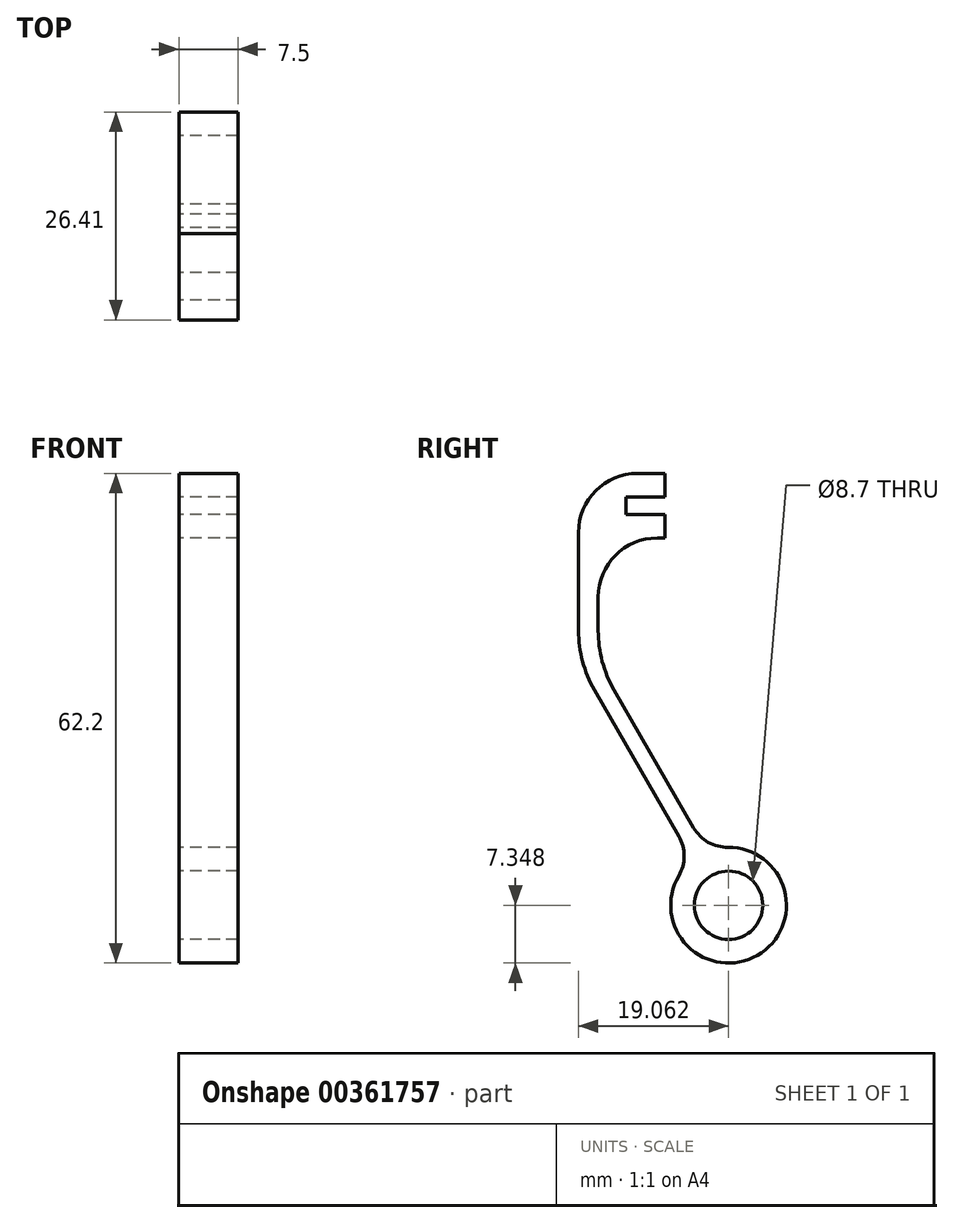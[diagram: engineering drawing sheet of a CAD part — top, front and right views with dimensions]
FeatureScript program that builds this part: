
annotation { "Feature Type Name" : "Feature", "Feature Type Description" : "" }
export const myFeature = defineFeature(function(context is Context, id is Id, definition is map)
    precondition{}
    {
        {
            var Q0;
            Q0=qCreatedBy(makeId("Right.planeOp"),FACE);
            var sketch = newSketch(context, id + "F0", { "sketchPlane" : qUnion([Q0])});
            skLineSegment(sketch, "E0", {"start": v(0, 18.8) * mm, "end": v(-5, 18.8) * mm});
            skLineSegment(sketch, "E1", {"start": v(-5, 18.8) * mm, "end": v(-5, 21) * mm});
            skLineSegment(sketch, "E2", {"start": v(-5, 21) * mm, "end": v(0, 21) * mm});
            skLineSegment(sketch, "E3", {"start": v(0, 21) * mm, "end": v(0, 24) * mm});
            skLineSegment(sketch, "E4", {"start": v(0, 24) * mm, "end": v(-11, 24) * mm});
            skLineSegment(sketch, "E5", {"start": v(0, 18.8) * mm, "end": v(0, 15.8) * mm});
            skLineSegment(sketch, "E6", {"start": v(0, 15.8) * mm, "end": v(-8.5, 15.8) * mm});
            skLineSegment(sketch, "E7", {"start": v(-8.5, 15.8) * mm, "end": v(-8.5, 4.02) * mm});
            skLineSegment(sketch, "E8", {"start": v(-6.5, -3.48) * mm, "end": v(3.63, -21) * mm});
            skLineSegment(sketch, "E9", {"start": v(-11, 24) * mm, "end": v(-11, 4.02) * mm});
            skLineSegment(sketch, "E10", {"start": v(-9, -3.48) * mm, "end": v(1.75, -22.09) * mm});
            skPoint(sketch, "E11.start.orphan", {"position": v(-16.86, 0) * mm});
            skPoint(sketch, "E12.orphan", {"position": v(6.83, -31.85) * mm});
            skPoint(sketch, "E13.orphan", {"position": v(7.4, -31.85) * mm});
            skCircle(sketch, "E14", {"center": v(8.06, -30.85) * mm, "radius": 4.35 * mm});
            skArc(sketch, "E15.0", {"start": v(1.73, -27.12) * mm, "mid": v(11.74, -37.22) * mm, "end": v(8, -23.5) * mm});
            skPoint(sketch, "E16.orphan", {"position": v(9, -30.31) * mm});
            skPoint(sketch, "E17.end.orphan", {"position": v(7.13, -31.4) * mm});
            skPoint(sketch, "E18.visualSharp", {"position": v(3.5, -25.1) * mm});
            skArc(sketch, "E18.filletArc", {"start": v(1.73, -27.12) * mm, "mid": v(2.42, -24.6) * mm, "end": v(1.75, -22.09) * mm});
            skPoint(sketch, "E19.visualSharp", {"position": v(5.37, -24.02) * mm});
            skArc(sketch, "E19.filletArc", {"start": v(3.63, -21) * mm, "mid": v(5.47, -22.84) * mm, "end": v(8, -23.5) * mm});
            skPoint(sketch, "E20.visualSharp", {"position": v(-8.5, 0) * mm});
            skArc(sketch, "E20.filletArc", {"start": v(-8.5, 4.02) * mm, "mid": v(-7.99, 0.14) * mm, "end": v(-6.5, -3.48) * mm});
            skPoint(sketch, "E21.visualSharp", {"position": v(-11, 0) * mm});
            skArc(sketch, "E21.filletArc", {"start": v(-11, 4.02) * mm, "mid": v(-10.49, 0.14) * mm, "end": v(-9, -3.48) * mm});
            skSolve(sketch);
        }
        {
            var Q0;
            Q0=makeQuery(id+"F0.imprint","IMPRINT",FACE,{"disambiguationData":[TD([[makeQuery(id+"F0.imprint","IMPRINT",EDGE,{"derivedFrom":sQuery(id+"F0.wireOp",EDGE,"E0")}),1.0]])]});
            extrude(context, id + "F1", {"entities" : qUnion([Q0]), "depth" : 7.5 * mm, "offsetDistance" : 25 * mm});
        }
        {
            var Q0;
            Q0=makeQuery(id+"F1.opExtrude","SWEPT_EDGE",EDGE,{"disambiguationData":[OSD([sQuery(id+"F0.wireOp",EDGE,"E4"),sQuery(id+"F0.wireOp",EDGE,"E9")])]});
            var Q1;
            Q1=makeQuery(id+"F1.opExtrude","SWEPT_EDGE",EDGE,{"disambiguationData":[OSD([sQuery(id+"F0.wireOp",EDGE,"E6"),sQuery(id+"F0.wireOp",EDGE,"E7")])]});
            fillet(context, id + "F2", {"entities" : qUnion([Q0, Q1]), "radius" : 7.5 * mm, "tangentPropagation" : true, "allowEdgeOverflow" : false});
        }
    });
